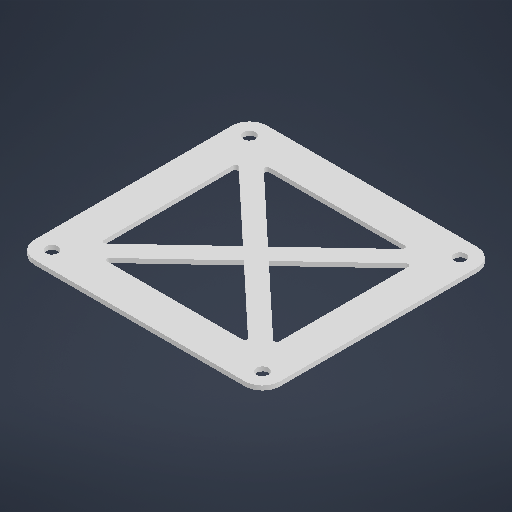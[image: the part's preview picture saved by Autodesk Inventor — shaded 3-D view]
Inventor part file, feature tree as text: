
AUTODESK INVENTOR PART (.ipt)
format: ipt  version: 2025.2 (Build 292293000, 293)  size: 241,664 bytes
history: native  units: in
note: dims shown in document units (in); Inventor stores cm internally (conversion verified against a paired STEP export)
features: extrude x1, sketch x1
ambient origin geometry x8: Origin, YZ Plane, XZ Plane, XY Plane, X Axis, Y Axis, Z Axis, Center Point
bodies: Solid1 (feature_tree)
feature tree (2):
  extrude  "Extrusion1"  Depth=0.5in
  sketch  "Sketch1"  dims[d0=0.5in d1=0.5in d2=0.5in d3=0.5in d8=0.25in d11=0.25in d14=0.25in d16=0.25in d17=0.25in d18=0.25in d19=0.25in d20=0.25in d21=0.035in d22=0.035in d23=0.035in d24=0.035in d25=0.035in d26=0.035in d27=0.035in d28=0.035in d29=0.0625in d30=0.0in]
